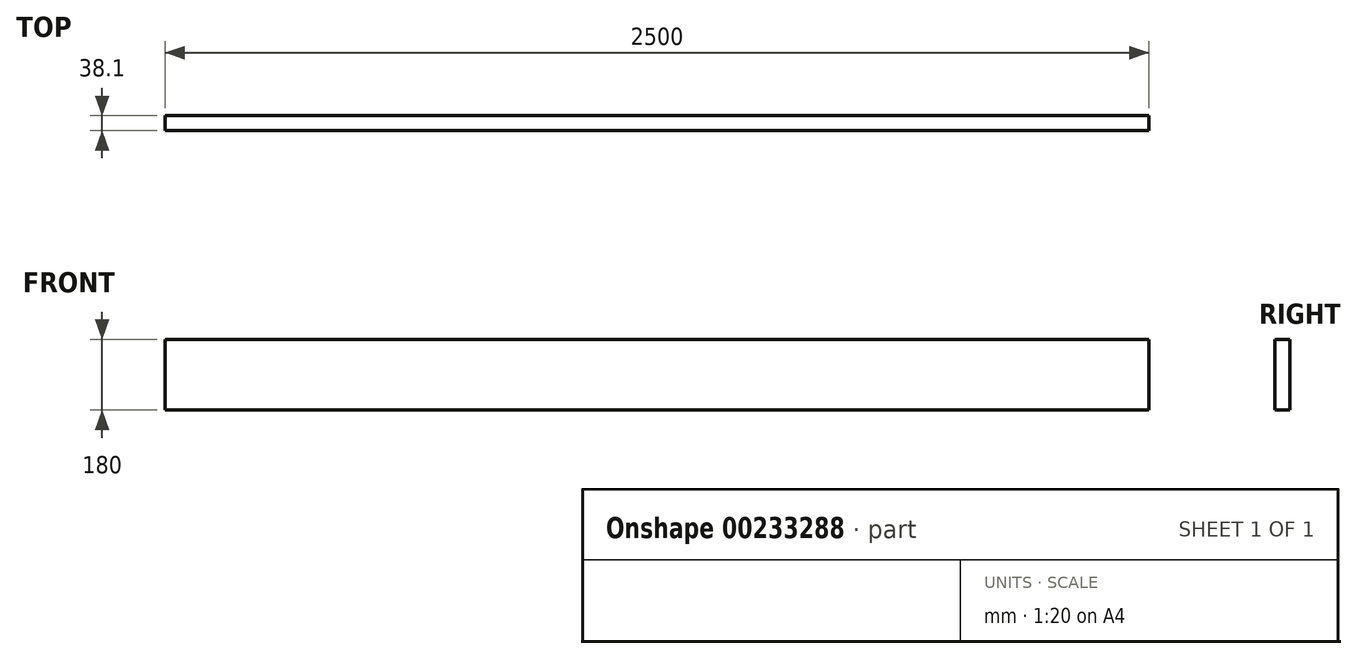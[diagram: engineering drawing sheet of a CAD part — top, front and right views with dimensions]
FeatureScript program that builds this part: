
annotation { "Feature Type Name" : "Feature", "Feature Type Description" : "" }
export const myFeature = defineFeature(function(context is Context, id is Id, definition is map)
    precondition{}
    {
        {
            var Q0;
            Q0=qCreatedBy(makeId("Front.planeOp"),FACE);
            var sketch = newSketch(context, id + "F0", { "sketchPlane" : qUnion([Q0])});
            skLineSegment(sketch, "E0.bottom", {"start": v(-1253.54, -182.25) * mm, "end": v(1246.46, -182.25) * mm});
            skLineSegment(sketch, "E0.top", {"start": v(-1253.54, -362.25) * mm, "end": v(1246.46, -362.25) * mm});
            skLineSegment(sketch, "E0.left", {"start": v(-1253.54, -182.25) * mm, "end": v(-1253.54, -362.25) * mm});
            skLineSegment(sketch, "E0.right", {"start": v(1246.46, -182.25) * mm, "end": v(1246.46, -362.25) * mm});
            skSolve(sketch);
        }
        {
            var Q0;
            Q0=makeQuery(id+"F0.imprint","IMPRINT",FACE,{"disambiguationData":[TD([[makeQuery(id+"F0.imprint","IMPRINT",EDGE,{"derivedFrom":sQuery(id+"F0.wireOp",EDGE,"E0.bottom")}),-1.0]])]});
            extrude(context, id + "F1", {"entities" : qUnion([Q0]), "depth" : 38.1 * mm});
        }
    });
